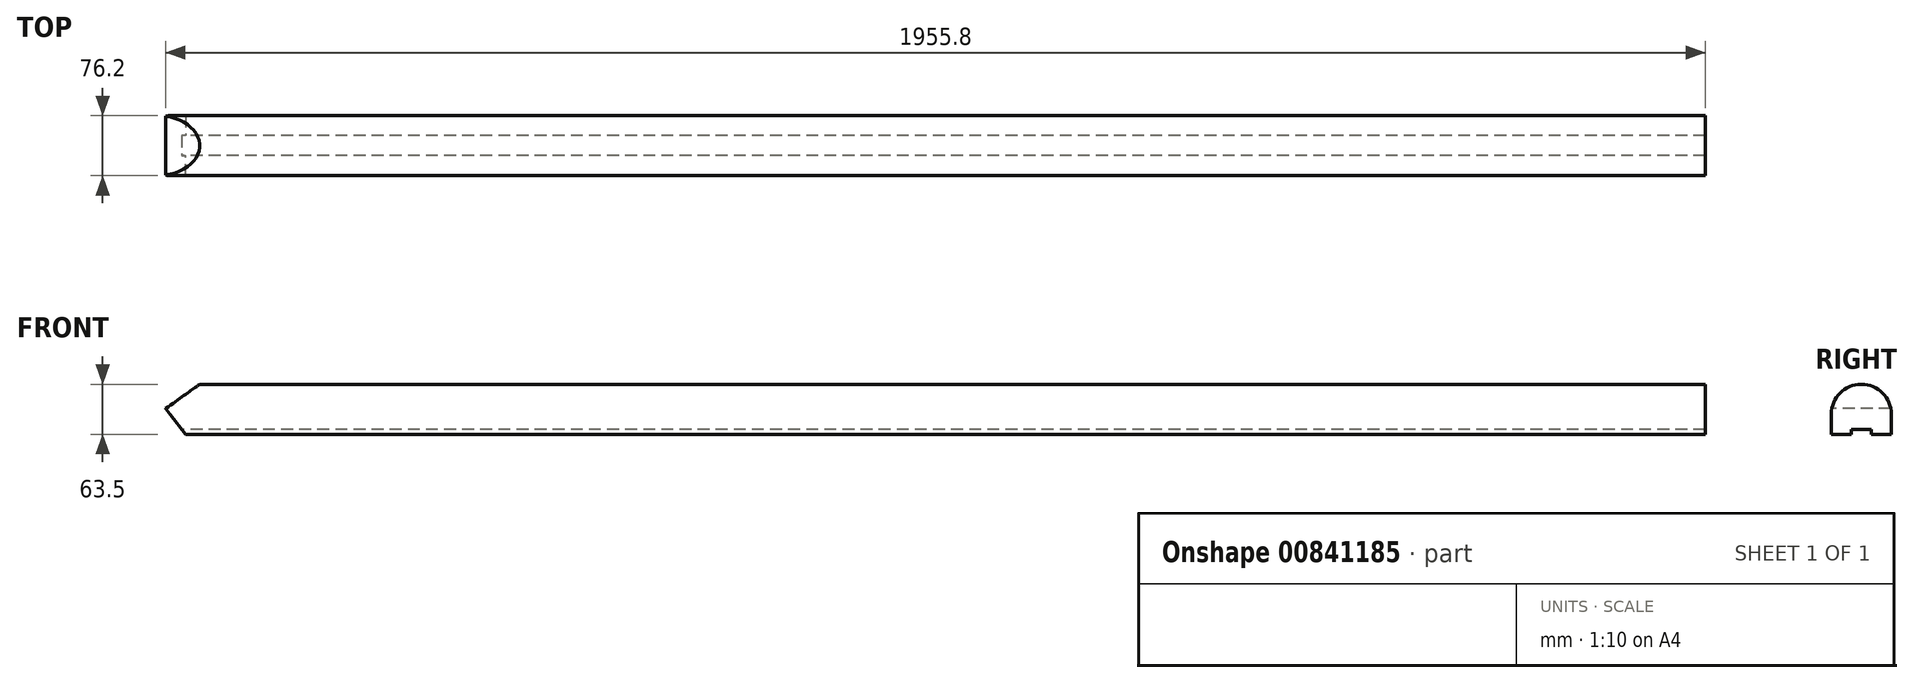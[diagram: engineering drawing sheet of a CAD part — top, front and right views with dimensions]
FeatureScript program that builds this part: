
annotation { "Feature Type Name" : "Feature", "Feature Type Description" : "" }
export const myFeature = defineFeature(function(context is Context, id is Id, definition is map)
    precondition{}
    {
        {
            var Q0;
            Q0=qCreatedBy(makeId("Right.planeOp"),FACE);
            var sketch = newSketch(context, id + "F0", { "sketchPlane" : qUnion([Q0])});
            skLineSegment(sketch, "E0.top", {"start": v(0, -25.4) * mm, "end": v(25.4, -25.4) * mm});
            skLineSegment(sketch, "E0.left", {"start": v(0, 0) * mm, "end": v(0, -25.4) * mm});
            skLineSegment(sketch, "E0.right", {"start": v(76.2, 0) * mm, "end": v(76.2, -25.4) * mm});
            skArc(sketch, "E1", {"start": v(76.2, 0) * mm, "mid": v(38.1, 38.1) * mm, "end": v(0, 0) * mm});
            skLineSegment(sketch, "E2", {"start": v(50.8, -25.4) * mm, "end": v(50.8, -19.05) * mm});
            skLineSegment(sketch, "E3", {"start": v(50.8, -19.05) * mm, "end": v(25.4, -19.05) * mm});
            skLineSegment(sketch, "E4", {"start": v(25.4, -19.05) * mm, "end": v(25.4, -25.4) * mm});
            skLineSegment(sketch, "E5.trimOffspring", {"start": v(50.8, -25.4) * mm, "end": v(76.2, -25.4) * mm});
            skSolve(sketch);
        }
        {
            var Q0;
            Q0=makeQuery(id+"F0.imprint","IMPRINT",FACE,{"disambiguationData":[TD([[makeQuery(id+"F0.imprint","IMPRINT",EDGE,{"derivedFrom":sQuery(id+"F0.wireOp",EDGE,"E0.top")}),1.0]])]});
            var Q1;
            Q1=makeQuery(id+"F0.imprint","IMPRINT",FACE,{"disambiguationData":[TD([[makeQuery(id+"F0.imprint","IMPRINT",EDGE,{"derivedFrom":sQuery(id+"F0.wireOp",EDGE,"xvRyiSZ1-6Cml-VsC9-tYd2-puqlQOu37wz5.bottom")}),-1.0]])]});
            extrude(context, id + "F1", {"entities" : qUnion([Q0, Q1]), "depth" : 1955.8 * mm, "offsetDistance" : 25.4 * mm});
        }
        {
            var Q0;
            Q0=makeQuery(id+"F1.opExtrude","CAP_EDGE",EDGE,{"disambiguationData":[OSD([sQuery(id+"F0.wireOp",EDGE,"E0.top")])],"isStart":true});
            chamfer(context, id + "F2", {"entities" : qUnion([Q0]), "chamferType" : ChamferType.OFFSET_ANGLE, "width" : 25.4 * mm, "oppositeDirection" : false, "angle" : 52 * degree, "tangentPropagation" : true});
        }
        {
            var Q0;
            Q0=qCreatedBy(makeId("Front.planeOp"),FACE);
            var sketch = newSketch(context, id + "F3", { "sketchPlane" : qUnion([Q0])});
            skLineSegment(sketch, "E6", {"start": v(17.98, 50.45) * mm, "end": v(0, 45.54) * mm});
            skLineSegment(sketch, "E7", {"start": v(0, 7.11) * mm, "end": v(44.91, 39.25) * mm});
            skLineSegment(sketch, "E8", {"start": v(0, 7.11) * mm, "end": v(0, 45.54) * mm});
            skLineSegment(sketch, "E9", {"start": v(17.98, 50.45) * mm, "end": v(44.91, 39.25) * mm});
            skSolve(sketch);
        }
        {
            var Q0;
            Q0=makeQuery(id+"F3.imprint","IMPRINT",FACE,{"disambiguationData":[TD([[makeQuery(id+"F3.imprint","IMPRINT",EDGE,{"derivedFrom":sQuery(id+"F3.wireOp",EDGE,"E6")}),1.0]])]});
            extrude(context, id + "F4", {"entities" : qUnion([Q0]), "operationType" : NewBodyOperationType.REMOVE, "endBound" : BoundingType.THROUGH_ALL, "oppositeDirection" : true, "depth" : 25.4 * mm, "offsetDistance" : 25.4 * mm});
        }
    });
